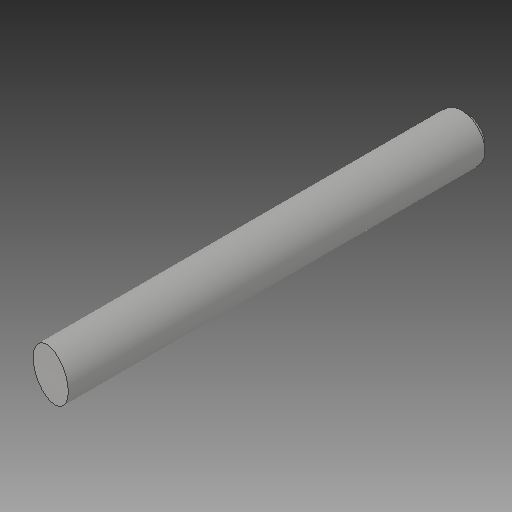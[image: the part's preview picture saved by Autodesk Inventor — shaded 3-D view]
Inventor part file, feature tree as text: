
AUTODESK INVENTOR PART (.ipt)
format: ipt  version: 2018 (Build 220112000, 112)  size: 130,560 bytes
history: native  units: mm
features: extrude x3, sketch x3, other x1, chamfer x1, projected_geometry x1
ambient origin geometry x8: Origin, YZ Plane, XZ Plane, XY Plane, X Axis, Y Axis, Z Axis, Center Point
bodies: Solid1 (feature_tree)
feature tree (9):
  parser-record x1  (decoder bookkeeping rows leaked as tree rows — omitted from the tree; the rows remain in map.json)
  extrude  "Extrusion1"  Depth=228.0mm
  extrude  "Extrusion2"  Depth=10.0mm TaperAngle=0.0deg
  extrude  "Extrusion3"  Depth=10.0mm
  chamfer  "Chamfer1"  Distance=10.0mm
  sketch  "Sketch1"  dims[d0=25.0mm d1=228.0mm]
  sketch  "Sketch2"  dims[d2=0.0mm d3=10.0mm d4=0.0mm]
  projected_geometry  "Projected Loop1"
  sketch  "Sketch3"  dims[d5=2.460914mm d6=2.953mm d7=10.0mm d8=0.0mm d9=3.0mm d10=2.0mm d11=45.0deg]
note: 1 file-system path scrubbed to <path> (originals preserved in map.json)
